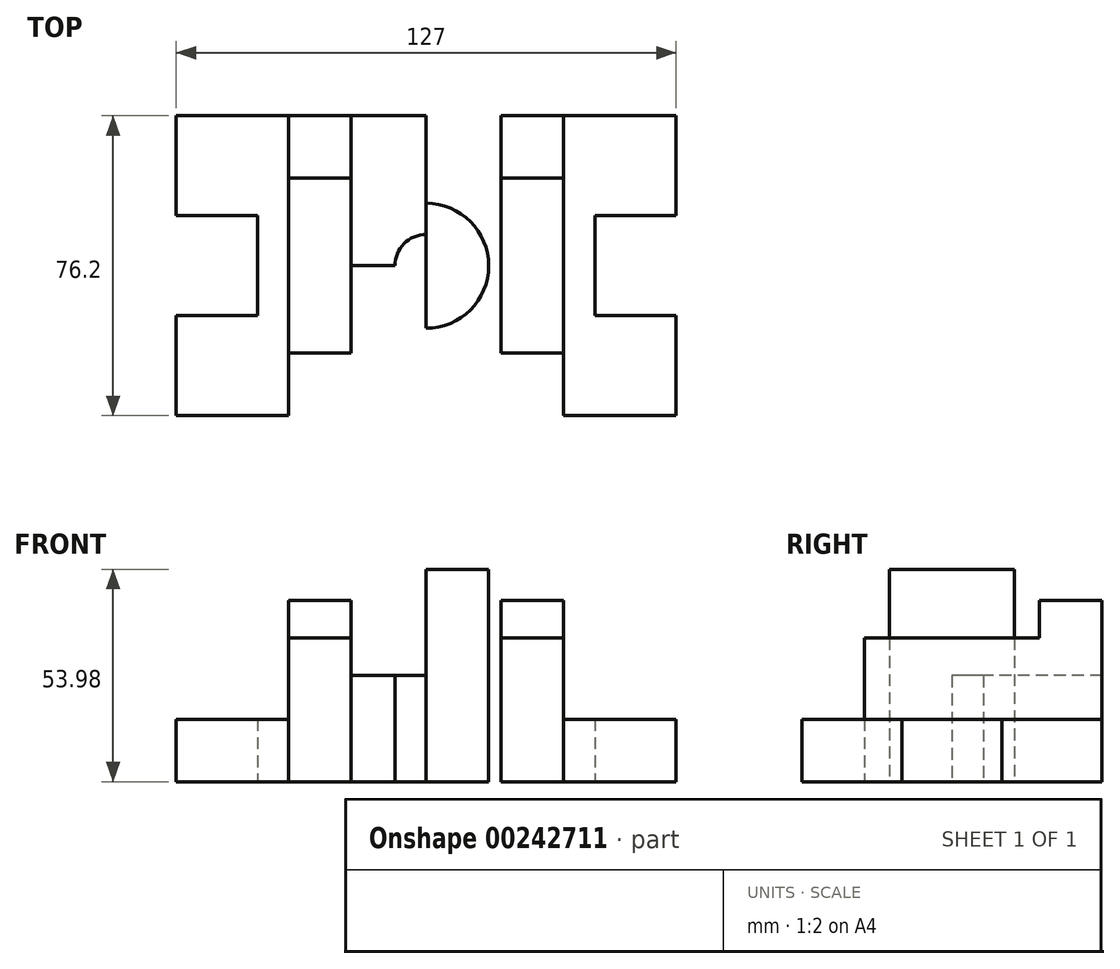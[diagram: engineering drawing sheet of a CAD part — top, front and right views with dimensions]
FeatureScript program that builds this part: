
annotation { "Feature Type Name" : "Feature", "Feature Type Description" : "" }
export const myFeature = defineFeature(function(context is Context, id is Id, definition is map)
    precondition{}
    {
        {
            var Q0;
            Q0=qCreatedBy(makeId("Top.planeOp"),FACE);
            var sketch = newSketch(context, id + "F0", { "sketchPlane" : qUnion([Q0])});
            skLineSegment(sketch, "E0.bottom", {"start": v(127, 76.2) * mm, "end": v(-127, 76.2) * mm});
            skLineSegment(sketch, "E0.top", {"start": v(127, -76.2) * mm, "end": v(-127, -76.2) * mm});
            skLineSegment(sketch, "E0.left", {"start": v(127, 76.2) * mm, "end": v(127, -76.2) * mm});
            skLineSegment(sketch, "E0.right", {"start": v(-127, 76.2) * mm, "end": v(-127, -76.2) * mm});
            skPoint(sketch, "E0.middle", {"position": v(0, 0) * mm});
            skLineSegment(sketch, "E1.bottom", {"start": v(127, 25.4) * mm, "end": v(85.72, 25.4) * mm});
            skLineSegment(sketch, "E1.top", {"start": v(127, -25.4) * mm, "end": v(85.73, -25.4) * mm});
            skLineSegment(sketch, "E1.left", {"start": v(127, 25.4) * mm, "end": v(127, -25.4) * mm});
            skLineSegment(sketch, "E1.right", {"start": v(85.73, 25.4) * mm, "end": v(85.73, -25.4) * mm});
            skPoint(sketch, "E1.middle", {"position": v(106.36, 0) * mm});
            skLineSegment(sketch, "E2.bottom", {"start": v(69.85, 76.2) * mm, "end": v(-69.85, 76.2) * mm});
            skLineSegment(sketch, "E2.top", {"start": v(69.85, -76.2) * mm, "end": v(-69.85, -76.2) * mm});
            skLineSegment(sketch, "E2.left", {"start": v(69.85, 76.2) * mm, "end": v(69.85, -76.2) * mm});
            skLineSegment(sketch, "E2.right", {"start": v(-69.85, 76.2) * mm, "end": v(-69.85, -76.2) * mm});
            skLineSegment(sketch, "E3.bottom", {"start": v(38.1, 76.2) * mm, "end": v(-38.1, 76.2) * mm});
            skLineSegment(sketch, "E3.top", {"start": v(38.1, -76.2) * mm, "end": v(-38.1, -76.2) * mm});
            skLineSegment(sketch, "E3.left", {"start": v(38.1, 76.2) * mm, "end": v(38.1, -76.2) * mm});
            skLineSegment(sketch, "E3.right", {"start": v(-38.1, 76.2) * mm, "end": v(-38.1, -76.2) * mm});
            skLineSegment(sketch, "E4.bottom", {"start": v(-69.85, -76.2) * mm, "end": v(-38.1, -76.2) * mm});
            skLineSegment(sketch, "E4.top", {"start": v(-69.85, -44.45) * mm, "end": v(-38.1, -44.45) * mm});
            skLineSegment(sketch, "E4.left", {"start": v(-69.85, -76.2) * mm, "end": v(-69.85, -44.45) * mm});
            skLineSegment(sketch, "E4.right", {"start": v(-38.1, -76.2) * mm, "end": v(-38.1, -44.45) * mm});
            skLineSegment(sketch, "E5", {"start": v(0, 76.2) * mm, "end": v(0, -76.2) * mm});
            skLineSegment(sketch, "E6", {"start": v(-127, 0) * mm, "end": v(127, 0) * mm});
            skCircle(sketch, "E7", {"center": v(0, 0) * mm, "radius": 15.88 * mm});
            skLineSegment(sketch, "E8.MirrorCS", {"start": v(-127, 25.4) * mm, "end": v(-85.72, 25.4) * mm});
            skLineSegment(sketch, "E9.MirrorCS", {"start": v(-85.72, 25.4) * mm, "end": v(-85.73, -25.4) * mm});
            skLineSegment(sketch, "E10.MirrorCS", {"start": v(-127, -25.4) * mm, "end": v(-85.73, -25.4) * mm});
            skLineSegment(sketch, "E11.MirrorCS", {"start": v(69.85, -44.45) * mm, "end": v(38.1, -44.45) * mm});
            skLineSegment(sketch, "E12.MirrorCS", {"start": v(69.85, 44.45) * mm, "end": v(38.1, 44.45) * mm});
            skLineSegment(sketch, "E13.MirrorCS", {"start": v(-69.85, 44.45) * mm, "end": v(-38.1, 44.45) * mm});
            skSolve(sketch);
        }
        {
            var Q0;
            {var subQ0=sQuery(id+"F0.wireOp",EDGE,"E8.MirrorCS");Q0=makeQuery(id+"F0.imprint","IMPRINT",FACE,{"disambiguationData":[TD([[makeQuery(id+"F0.imprint","IMPRINT",EDGE,{"derivedFrom":subQ0}),1.0]])]});}
            var Q1;
            {var subQ3=sQuery(id+"F0.wireOp",EDGE,"E10.MirrorCS");Q1=makeQuery(id+"F0.imprint","IMPRINT",FACE,{"disambiguationData":[TD([[makeQuery(id+"F0.imprint","IMPRINT",EDGE,{"derivedFrom":subQ3}),-1.0]])]});}
            var Q2;
            {var subQ1=sQuery(id+"F0.wireOp",EDGE,"E1.top");Q2=makeQuery(id+"F0.imprint","IMPRINT",FACE,{"disambiguationData":[TD([[makeQuery(id+"F0.imprint","IMPRINT",EDGE,{"derivedFrom":subQ1}),1.0]])]});}
            var Q3;
            {var subQ1=sQuery(id+"F0.wireOp",EDGE,"E1.bottom");Q3=makeQuery(id+"F0.imprint","IMPRINT",FACE,{"disambiguationData":[TD([[makeQuery(id+"F0.imprint","IMPRINT",EDGE,{"derivedFrom":subQ1}),-1.0]])]});}
            extrude(context, id + "F1", {"entities" : qUnion([Q0, Q1, Q2, Q3]), "depth" : 31.75 * mm});
        }
        {
            var Q0;
            {var subQ0=sQuery(id+"F0.wireOp",EDGE,"E4.bottom");Q0=makeQuery(id+"F0.imprint","IMPRINT",FACE,{"disambiguationData":[TD([[makeQuery(id+"F0.imprint","IMPRINT",EDGE,{"derivedFrom":subQ0}),1.0]])]});}
            var Q1;
            {var subQ5=sQuery(id+"F0.wireOp",EDGE,"E13.MirrorCS");Q1=makeQuery(id+"F0.imprint","IMPRINT",FACE,{"disambiguationData":[TD([[makeQuery(id+"F0.imprint","IMPRINT",EDGE,{"derivedFrom":subQ5}),1.0]])]});}
            var Q2;
            {var subQ5=sQuery(id+"F0.wireOp",EDGE,"E12.MirrorCS");Q2=makeQuery(id+"F0.imprint","IMPRINT",FACE,{"disambiguationData":[TD([[makeQuery(id+"F0.imprint","IMPRINT",EDGE,{"derivedFrom":subQ5}),-1.0]])]});}
            var Q3;
            {var subQ0=sQuery(id+"F0.wireOp",EDGE,"E2.top");Q3=makeQuery(id+"F0.imprint","IMPRINT",FACE,{"disambiguationData":[TD([[makeQuery(id+"F0.imprint","IMPRINT",EDGE,{"derivedFrom":subQ0}),-1.0]])]});}
            extrude(context, id + "F2", {"entities" : qUnion([Q0, Q1, Q2, Q3]), "operationType" : NewBodyOperationType.ADD, "depth" : 92.07 * mm});
        }
        {
            var Q0;
            {var subQ0=sQuery(id+"F0.wireOp",EDGE,"E13.MirrorCS");Q0=makeQuery(id+"F0.imprint","IMPRINT",FACE,{"disambiguationData":[TD([[makeQuery(id+"F0.imprint","IMPRINT",EDGE,{"derivedFrom":subQ0}),-1.0]])]});}
            var Q1;
            {var subQ0=sQuery(id+"F0.wireOp",EDGE,"E4.top");Q1=makeQuery(id+"F0.imprint","IMPRINT",FACE,{"disambiguationData":[TD([[makeQuery(id+"F0.imprint","IMPRINT",EDGE,{"derivedFrom":subQ0}),1.0]])]});}
            var Q2;
            {var subQ0=sQuery(id+"F0.wireOp",EDGE,"E12.MirrorCS");Q2=makeQuery(id+"F0.imprint","IMPRINT",FACE,{"disambiguationData":[TD([[makeQuery(id+"F0.imprint","IMPRINT",EDGE,{"derivedFrom":subQ0}),1.0]])]});}
            var Q3;
            {var subQ0=sQuery(id+"F0.wireOp",EDGE,"E11.MirrorCS");Q3=makeQuery(id+"F0.imprint","IMPRINT",FACE,{"disambiguationData":[TD([[makeQuery(id+"F0.imprint","IMPRINT",EDGE,{"derivedFrom":subQ0}),-1.0]])]});}
            extrude(context, id + "F3", {"entities" : qUnion([Q0, Q1, Q2, Q3]), "operationType" : NewBodyOperationType.ADD, "depth" : 73.02 * mm});
        }
        {
            var Q0;
            {var subQ6=sQuery(id+"F0.wireOp",EDGE,"E3.right");var subQ9=makeQuery(id+"F0.imprint","INTERSECT",VERTEX,{"derivedFrom":[subQ6,sQuery(id+"F0.wireOp",EDGE,"E13.MirrorCS")]});Q0=makeQuery(id+"F0.imprint","IMPRINT",FACE,{"disambiguationData":[TD([[makeQuery(id+"F0.imprint","IMPRINT",EDGE,{"disambiguationData":[TD([[subQ9,-1.0]])],"derivedFrom":subQ6}),1.0]])]});}
            var Q1;
            {var subQ1=sQuery(id+"F0.wireOp",EDGE,"E5");var subQ5=sQuery(id+"F0.wireOp",EDGE,"E3.bottom");var subQ6=makeQuery(id+"F0.imprint","INTERSECT",VERTEX,{"derivedFrom":[subQ5,subQ1]});Q1=makeQuery(id+"F0.imprint","IMPRINT",FACE,{"disambiguationData":[TD([[makeQuery(id+"F0.imprint","IMPRINT",EDGE,{"disambiguationData":[TD([[subQ6,-1.0]])],"derivedFrom":subQ1}),1.0]])]});}
            var Q2;
            {var subQ5=sQuery(id+"F0.wireOp",EDGE,"E5");var subQ6=sQuery(id+"F0.wireOp",EDGE,"E3.top");var subQ7=makeQuery(id+"F0.imprint","INTERSECT",VERTEX,{"derivedFrom":[subQ6,subQ5]});Q2=makeQuery(id+"F0.imprint","IMPRINT",FACE,{"disambiguationData":[TD([[makeQuery(id+"F0.imprint","IMPRINT",EDGE,{"disambiguationData":[TD([[subQ7,1.0]])],"derivedFrom":subQ5}),1.0]])]});}
            var Q3;
            {var subQ5=sQuery(id+"F0.wireOp",EDGE,"E4.right");Q3=makeQuery(id+"F0.imprint","IMPRINT",FACE,{"disambiguationData":[TD([[makeQuery(id+"F0.imprint","IMPRINT",EDGE,{"derivedFrom":subQ5}),-1.0]])]});}
            extrude(context, id + "F4", {"entities" : qUnion([Q0, Q1, Q2, Q3]), "operationType" : NewBodyOperationType.ADD, "depth" : 53.97 * mm});
        }
        {
            var Q0;
            Q0=makeQuery(id+"F1.opExtrude","SWEPT_BODY",BODY,{"disambiguationData":[OSD([sQuery(id+"F0.wireOp",EDGE,"E0.bottom"),sQuery(id+"F0.wireOp",EDGE,"E0.top"),sQuery(id+"F0.wireOp",EDGE,"E0.left"),sQuery(id+"F0.wireOp",EDGE,"E1.bottom"),sQuery(id+"F0.wireOp",EDGE,"E1.top"),sQuery(id+"F0.wireOp",EDGE,"E1.right"),sQuery(id+"F0.wireOp",EDGE,"E2.left")])]});
            var Q1;
            Q1=makeQuery(id+"F1.opExtrude","SWEPT_BODY",BODY,{"disambiguationData":[OSD([sQuery(id+"F0.wireOp",EDGE,"E0.bottom"),sQuery(id+"F0.wireOp",EDGE,"E0.top"),sQuery(id+"F0.wireOp",EDGE,"E0.right"),sQuery(id+"F0.wireOp",EDGE,"E8.MirrorCS"),sQuery(id+"F0.wireOp",EDGE,"E9.MirrorCS"),sQuery(id+"F0.wireOp",EDGE,"E10.MirrorCS"),sQuery(id+"F0.wireOp",EDGE,"E2.right")])]});
            var Q2;
            Q2=makeQuery(id+"F2.opExtrude","SWEPT_BODY",BODY,{"disambiguationData":[OSD([sQuery(id+"F0.wireOp",EDGE,"E2.bottom"),sQuery(id+"F0.wireOp",EDGE,"E2.left"),sQuery(id+"F0.wireOp",EDGE,"E3.left"),sQuery(id+"F0.wireOp",EDGE,"E12.MirrorCS")])]});
            var Q3;
            Q3=makeQuery(id+"F2.opExtrude","SWEPT_BODY",BODY,{"disambiguationData":[OSD([sQuery(id+"F0.wireOp",EDGE,"E2.bottom"),sQuery(id+"F0.wireOp",EDGE,"E3.right"),sQuery(id+"F0.wireOp",EDGE,"E2.right"),sQuery(id+"F0.wireOp",EDGE,"E13.MirrorCS")])]});
            var Q4;
            Q4=makeQuery(id+"F2.opExtrude","SWEPT_BODY",BODY,{"disambiguationData":[OSD([sQuery(id+"F0.wireOp",EDGE,"E2.top"),sQuery(id+"F0.wireOp",EDGE,"E2.left"),sQuery(id+"F0.wireOp",EDGE,"E11.MirrorCS"),sQuery(id+"F0.wireOp",EDGE,"E3.left")])]});
            var Q5;
            Q5=makeQuery(id+"F2.opExtrude","SWEPT_BODY",BODY,{"disambiguationData":[OSD([sQuery(id+"F0.wireOp",EDGE,"E4.bottom"),sQuery(id+"F0.wireOp",EDGE,"E4.top"),sQuery(id+"F0.wireOp",EDGE,"E4.right"),sQuery(id+"F0.wireOp",EDGE,"E2.right")])]});
            var Q6;
            Q6=makeQuery(id+"F3.opExtrude","SWEPT_BODY",BODY,{"disambiguationData":[OSD([sQuery(id+"F0.wireOp",EDGE,"E2.left"),sQuery(id+"F0.wireOp",EDGE,"E11.MirrorCS"),sQuery(id+"F0.wireOp",EDGE,"E3.left"),sQuery(id+"F0.wireOp",EDGE,"E12.MirrorCS")])]});
            var Q7;
            Q7=makeQuery(id+"F3.opExtrude","SWEPT_BODY",BODY,{"disambiguationData":[OSD([sQuery(id+"F0.wireOp",EDGE,"E3.right"),sQuery(id+"F0.wireOp",EDGE,"E4.top"),sQuery(id+"F0.wireOp",EDGE,"E2.right"),sQuery(id+"F0.wireOp",EDGE,"E13.MirrorCS")])]});
            var Q8;
            Q8=makeQuery(id+"F4.opExtrude","SWEPT_BODY",BODY,{"disambiguationData":[OSD([sQuery(id+"F0.wireOp",EDGE,"E3.bottom"),sQuery(id+"F0.wireOp",EDGE,"E3.top"),sQuery(id+"F0.wireOp",EDGE,"E3.right"),sQuery(id+"F0.wireOp",EDGE,"E4.right"),sQuery(id+"F0.wireOp",EDGE,"E7"),sQuery(id+"F0.wireOp",EDGE,"E3.left")])]});
            var Q9;
            Q9=qCreatedBy(makeId("Origin.pointOp"),VERTEX);
            var Q10;
            Q10=qCreatedBy(makeId("Origin.pointOp"),VERTEX);
            transform(context, id + "F5", {"entities" : qUnion([Q0, Q1, Q2, Q3, Q4, Q5, Q6, Q7, Q8]), "transformType" : TransformType.SCALE_UNIFORMLY, "scale" : 0.5, "scalePoint" : qUnion([Q10]), "makeCopy" : false});
        }
    });
